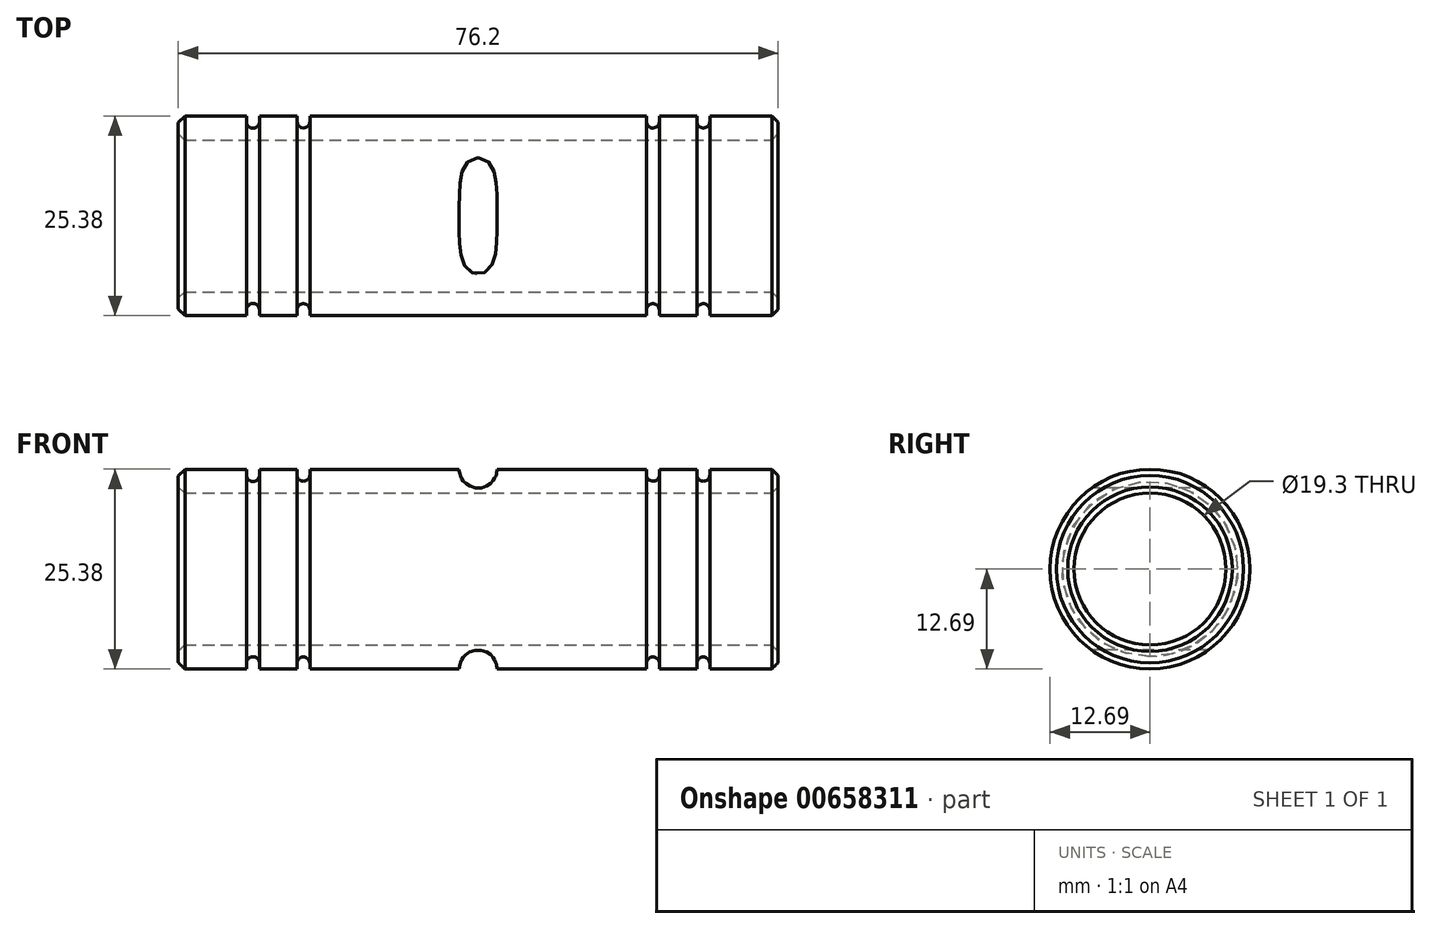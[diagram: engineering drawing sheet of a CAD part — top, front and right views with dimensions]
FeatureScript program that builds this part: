
annotation { "Feature Type Name" : "Feature", "Feature Type Description" : "" }
export const myFeature = defineFeature(function(context is Context, id is Id, definition is map)
    precondition{}
    {
        {
            var Q0;
            Q0=qCreatedBy(makeId("Front.planeOp"),FACE);
            var sketch = newSketch(context, id + "F0", { "sketchPlane" : qUnion([Q0])});
            skLineSegment(sketch, "E0", {"start": v(0, 0) * mm, "end": v(-61.8, 0) * mm});
            skLineSegment(sketch, "E1", {"start": v(0, 10.45) * mm, "end": v(0, 11.84) * mm});
            skLineSegment(sketch, "E2", {"start": v(0.85, 12.69) * mm, "end": v(8.67, 12.69) * mm});
            skLineSegment(sketch, "E3", {"start": v(76.2, 11.89) * mm, "end": v(76.2, 10.45) * mm});
            skLineSegment(sketch, "E4", {"start": v(75.4, 9.65) * mm, "end": v(0.8, 9.65) * mm});
            skArc(sketch, "E5", {"start": v(8.67, 11.95) * mm, "mid": v(9.5, 11.12) * mm, "end": v(10.33, 11.95) * mm});
            skArc(sketch, "E6", {"start": v(15.07, 11.99) * mm, "mid": v(15.9, 11.16) * mm, "end": v(16.73, 11.99) * mm});
            skArc(sketch, "E7", {"start": v(59.47, 11.99) * mm, "mid": v(60.3, 11.16) * mm, "end": v(61.13, 11.99) * mm});
            skLineSegment(sketch, "E8", {"start": v(8.67, 12.69) * mm, "end": v(8.67, 11.95) * mm});
            skLineSegment(sketch, "E9", {"start": v(10.33, 11.95) * mm, "end": v(10.33, 12.69) * mm});
            skLineSegment(sketch, "E10", {"start": v(15.07, 12.69) * mm, "end": v(15.07, 11.99) * mm});
            skLineSegment(sketch, "E11", {"start": v(16.73, 11.99) * mm, "end": v(16.73, 12.69) * mm});
            skLineSegment(sketch, "E12", {"start": v(59.47, 12.69) * mm, "end": v(59.47, 11.99) * mm});
            skLineSegment(sketch, "E13", {"start": v(61.13, 11.99) * mm, "end": v(61.13, 12.69) * mm});
            skLineSegment(sketch, "E14", {"start": v(65.87, 12.69) * mm, "end": v(65.87, 11.99) * mm});
            skLineSegment(sketch, "E15", {"start": v(67.53, 11.99) * mm, "end": v(67.53, 12.69) * mm});
            skLineSegment(sketch, "E16.trimOffspring", {"start": v(10.33, 12.69) * mm, "end": v(15.07, 12.69) * mm});
            skLineSegment(sketch, "E17.trimOffspring", {"start": v(16.73, 12.69) * mm, "end": v(35.64, 12.69) * mm});
            skLineSegment(sketch, "E18.trimOffspring", {"start": v(67.53, 12.69) * mm, "end": v(75.4, 12.69) * mm});
            skArc(sketch, "E19.trimOffspring", {"start": v(65.87, 11.99) * mm, "mid": v(66.7, 11.16) * mm, "end": v(67.53, 11.99) * mm});
            skLineSegment(sketch, "E20.trimOffspring", {"start": v(61.13, 12.69) * mm, "end": v(65.87, 12.69) * mm});
            skLineSegment(sketch, "E21.trimOffspring", {"start": v(40.56, 12.69) * mm, "end": v(59.47, 12.69) * mm});
            skLineSegment(sketch, "E22", {"start": v(75.4, 9.65) * mm, "end": v(76.2, 10.45) * mm});
            skLineSegment(sketch, "E23", {"start": v(0.8, 9.65) * mm, "end": v(0, 10.45) * mm});
            skPoint(sketch, "E24.orphan", {"position": v(76.2, 9.65) * mm});
            skPoint(sketch, "E25.orphan", {"position": v(0, 9.65) * mm});
            skLineSegment(sketch, "E26", {"start": v(0, 11.84) * mm, "end": v(0.85, 12.69) * mm});
            skPoint(sketch, "E27.orphan", {"position": v(0, 12.69) * mm});
            skLineSegment(sketch, "E28", {"start": v(75.4, 12.69) * mm, "end": v(76.2, 11.89) * mm});
            skPoint(sketch, "E29.orphan", {"position": v(76.2, 12.69) * mm});
            skLineSegment(sketch, "E30", {"start": v(35.64, 12.69) * mm, "end": v(40.56, 12.69) * mm});
            skPoint(sketch, "E31.center.orphan", {"position": v(38.1, 12.69) * mm});
            skSolve(sketch);
        }
        {
            var Q0;
            Q0=makeQuery(id+"F0.imprint","IMPRINT",FACE,{"disambiguationData":[TD([[makeQuery(id+"F0.imprint","IMPRINT",EDGE,{"derivedFrom":sQuery(id+"F0.wireOp",EDGE,"E1")}),-1.0]])]});
            var Q1;
            Q1=sQuery(id+"F0.wireOp",EDGE,"E0");
            revolve(context, id + "F1", {"entities" : qUnion([Q0]), "axis" : qUnion([Q1]), "revolveType" : RevolveType.FULL});
        }
        {
            var Q0;
            Q0=qCreatedBy(makeId("Front.planeOp"),FACE);
            var sketch = newSketch(context, id + "F2", { "sketchPlane" : qUnion([Q0])});
            skCircle(sketch, "E32", {"center": v(38.1, 12.69) * mm, "radius": 2.4 * mm});
            skCircle(sketch, "E33", {"center": v(38.1, -12.69) * mm, "radius": 2.4 * mm});
            skSolve(sketch);
        }
        {
            var Q0;
            Q0 = qSketchRegion(id + "F2", true);
            extrude(context, id + "F3", {"entities" : qUnion([Q0]), "operationType" : NewBodyOperationType.REMOVE, "endBound" : BoundingType.THROUGH_ALL, "oppositeDirection" : true, "depth" : 25.4 * mm, "offsetDistance" : 25.4 * mm, "hasSecondDirection" : true, "secondDirectionBound" : SecondDirectionBoundingType.THROUGH_ALL, "secondDirectionOppositeDirection" : false, "secondDirectionDepth" : 25.4 * mm});
        }
    });
